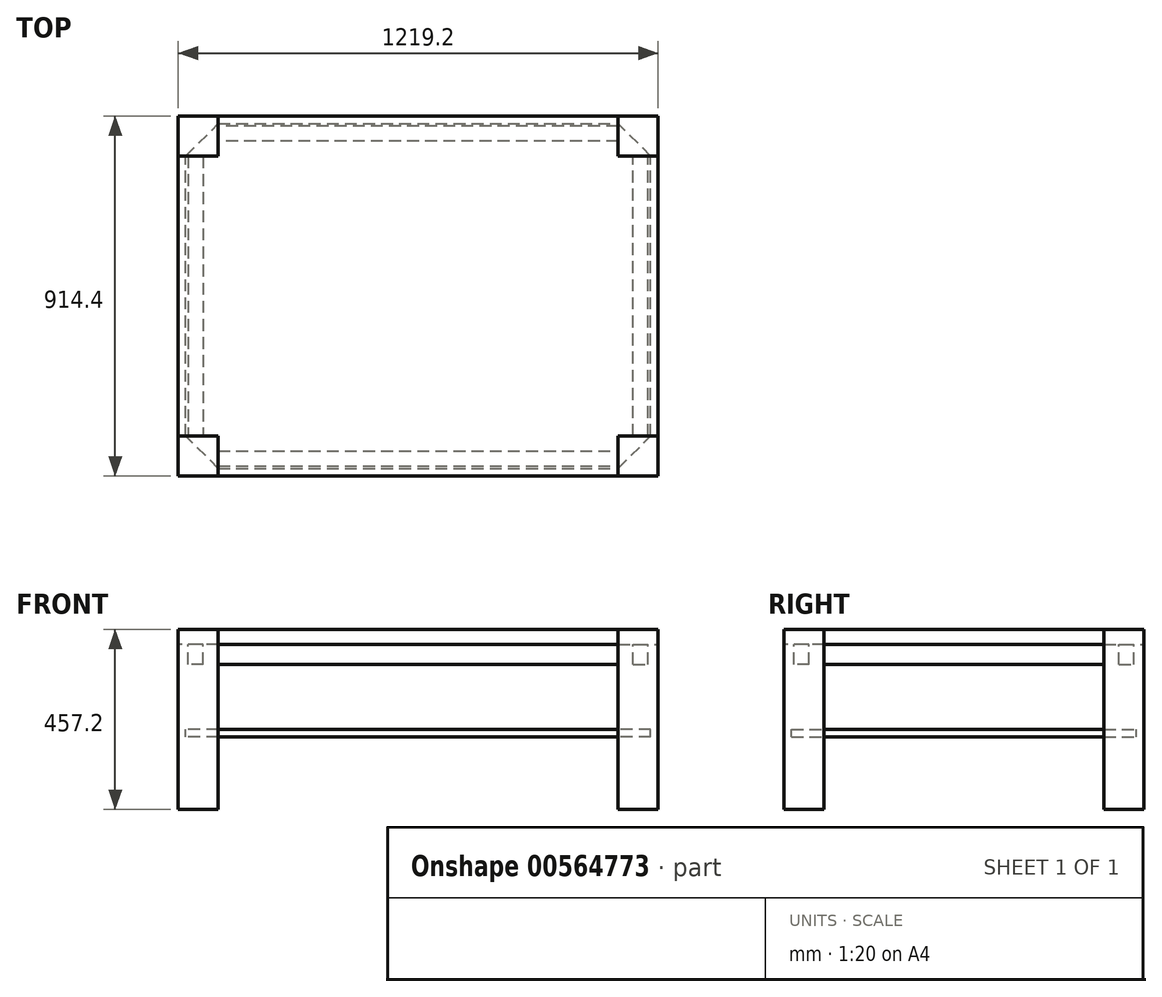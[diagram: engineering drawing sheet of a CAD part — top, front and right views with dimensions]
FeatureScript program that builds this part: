
annotation { "Feature Type Name" : "Feature", "Feature Type Description" : "" }
export const myFeature = defineFeature(function(context is Context, id is Id, definition is map)
    precondition{}
    {
        {
            assignVariable(context, id + "F0", {"name" : "height", "anyValue" : 457.2 * mm});
        }
        {
            assignVariable(context, id + "F1", {"name" : "shelf_height", "anyValue" : 203.2 * mm});
        }
        {
            var Q0;
            Q0=qCreatedBy(makeId("Top.planeOp"),FACE);
            var sketch = newSketch(context, id + "F2", { "sketchPlane" : qUnion([Q0])});
            skPoint(sketch, "E0.middle", {"position": v(0, 0) * mm});
            skLineSegment(sketch, "E1", {"start": v(-609.6, 355.6) * mm, "end": v(-609.6, -355.6) * mm});
            skLineSegment(sketch, "E2", {"start": v(-609.6, -355.6) * mm, "end": v(-508, -355.6) * mm});
            skLineSegment(sketch, "E3", {"start": v(-508, -355.6) * mm, "end": v(-508, -457.2) * mm});
            skLineSegment(sketch, "E4", {"start": v(-508, -457.2) * mm, "end": v(508, -457.2) * mm});
            skLineSegment(sketch, "E5", {"start": v(508, -457.2) * mm, "end": v(508, -355.6) * mm});
            skLineSegment(sketch, "E6", {"start": v(508, -355.6) * mm, "end": v(609.6, -355.6) * mm});
            skLineSegment(sketch, "E7", {"start": v(609.6, -355.6) * mm, "end": v(609.6, 355.6) * mm});
            skLineSegment(sketch, "E8", {"start": v(609.6, 355.6) * mm, "end": v(508, 355.6) * mm});
            skLineSegment(sketch, "E9", {"start": v(508, 355.6) * mm, "end": v(508, 457.2) * mm});
            skLineSegment(sketch, "E10", {"start": v(508, 457.2) * mm, "end": v(-508, 457.2) * mm});
            skLineSegment(sketch, "E11", {"start": v(-508, 457.2) * mm, "end": v(-508, 355.6) * mm});
            skLineSegment(sketch, "E12", {"start": v(-508, 355.6) * mm, "end": v(-609.6, 355.6) * mm});
            skLineSegment(sketch, "E13", {"start": v(-508, 355.6) * mm, "end": v(508, -355.6) * mm, "construction": true});
            skLineSegment(sketch, "E14", {"start": v(508, 355.6) * mm, "end": v(-508, -355.6) * mm, "construction": true});
            skSolve(sketch);
        }
        {
            var Q0;
            Q0 = qSketchRegion(id + "F2", true);
            extrude(context, id + "F3", {"entities" : qUnion([Q0]), "depth" : 38.1 * mm, "offsetDistance" : 25.4 * mm});
        }
        {
            var Q0;
            Q0=makeQuery(id+"F3.opExtrude","CAP_FACE",FACE,{"disambiguationData":[OSD([sQuery(id+"F2.wireOp",EDGE,"E1"),sQuery(id+"F2.wireOp",EDGE,"E2"),sQuery(id+"F2.wireOp",EDGE,"E3"),sQuery(id+"F2.wireOp",EDGE,"E4"),sQuery(id+"F2.wireOp",EDGE,"E5"),sQuery(id+"F2.wireOp",EDGE,"E6"),sQuery(id+"F2.wireOp",EDGE,"E7"),sQuery(id+"F2.wireOp",EDGE,"E8"),sQuery(id+"F2.wireOp",EDGE,"E9"),sQuery(id+"F2.wireOp",EDGE,"E10"),sQuery(id+"F2.wireOp",EDGE,"E11"),sQuery(id+"F2.wireOp",EDGE,"E12")])],"isStart":false});
            var sketch = newSketch(context, id + "F4", { "sketchPlane" : qUnion([Q0])});
            skLineSegment(sketch, "E15.bottom", {"start": v(-609.6, -355.6) * mm, "end": v(-508, -355.6) * mm});
            skLineSegment(sketch, "E15.top", {"start": v(-609.6, -457.2) * mm, "end": v(-508, -457.2) * mm});
            skLineSegment(sketch, "E15.left", {"start": v(-609.6, -355.6) * mm, "end": v(-609.6, -457.2) * mm});
            skLineSegment(sketch, "E15.right", {"start": v(-508, -355.6) * mm, "end": v(-508, -457.2) * mm});
            skLineSegment(sketch, "E16.bottom", {"start": v(508, -457.2) * mm, "end": v(609.6, -457.2) * mm});
            skLineSegment(sketch, "E16.top", {"start": v(508, -355.6) * mm, "end": v(609.6, -355.6) * mm});
            skLineSegment(sketch, "E16.left", {"start": v(508, -457.2) * mm, "end": v(508, -355.6) * mm});
            skLineSegment(sketch, "E16.right", {"start": v(609.6, -457.2) * mm, "end": v(609.6, -355.6) * mm});
            skLineSegment(sketch, "E17.bottom", {"start": v(609.6, 355.6) * mm, "end": v(508, 355.6) * mm});
            skLineSegment(sketch, "E17.top", {"start": v(609.6, 457.2) * mm, "end": v(508, 457.2) * mm});
            skLineSegment(sketch, "E17.left", {"start": v(609.6, 355.6) * mm, "end": v(609.6, 457.2) * mm});
            skLineSegment(sketch, "E17.right", {"start": v(508, 355.6) * mm, "end": v(508, 457.2) * mm});
            skLineSegment(sketch, "E18.bottom", {"start": v(-508, 457.2) * mm, "end": v(-609.6, 457.2) * mm});
            skLineSegment(sketch, "E18.top", {"start": v(-508, 355.6) * mm, "end": v(-609.6, 355.6) * mm});
            skLineSegment(sketch, "E18.left", {"start": v(-508, 457.2) * mm, "end": v(-508, 355.6) * mm});
            skLineSegment(sketch, "E18.right", {"start": v(-609.6, 457.2) * mm, "end": v(-609.6, 355.6) * mm});
            skSolve(sketch);
        }
        {
            var Q0;
            Q0 = qSketchRegion(id + "F4", true);
            extrude(context, id + "F5", {"entities" : qUnion([Q0]), "oppositeDirection" : true, "depth" : getVariable(context, 'height'), "offsetDistance" : 25.4 * mm});
        }
        {
            var Q0;
            Q0=makeQuery(id+"F5.opExtrude","CAP_FACE",FACE,{"disambiguationData":[OSD([sQuery(id+"F4.wireOp",EDGE,"E15.bottom"),sQuery(id+"F4.wireOp",EDGE,"E15.top"),sQuery(id+"F4.wireOp",EDGE,"E15.left"),sQuery(id+"F4.wireOp",EDGE,"E15.right")])],"isStart":false});
            cPlane(context, id + "F6", {"entities" : qUnion([Q0]), "cplaneType" : CPlaneType.OFFSET, "offset" : getVariable(context, 'shelf_height'), "oppositeDirection" : true, "width" : 152.4 * mm, "height" : 152.4 * mm});
        }
        {
            var Q0;
            Q0=qCreatedBy(id+"F6.planeOp",FACE);
            var sketch = newSketch(context, id + "F7", { "sketchPlane" : qUnion([Q0])});
            skLineSegment(sketch, "E19.bottom", {"start": v(-590.5, 438.1) * mm, "end": v(590.5, 438.1) * mm});
            skLineSegment(sketch, "E19.top", {"start": v(-590.5, -438.1) * mm, "end": v(590.5, -438.1) * mm});
            skLineSegment(sketch, "E19.left", {"start": v(-590.5, 438.1) * mm, "end": v(-590.5, -438.1) * mm});
            skLineSegment(sketch, "E19.right", {"start": v(590.5, 438.1) * mm, "end": v(590.5, -438.1) * mm});
            skLineSegment(sketch, "E20", {"start": v(-508, 438.1) * mm, "end": v(-590.5, 355.6) * mm});
            skLineSegment(sketch, "E21", {"start": v(508, 438.1) * mm, "end": v(590.5, 355.6) * mm});
            skLineSegment(sketch, "E22", {"start": v(590.5, -355.6) * mm, "end": v(508, -438.1) * mm});
            skLineSegment(sketch, "E23", {"start": v(-590.5, -355.6) * mm, "end": v(-508, -438.1) * mm});
            skSolve(sketch);
        }
        {
            var Q0;
            {var subQ3=sQuery(id+"F7.wireOp",EDGE,"E20");Q0=makeQuery(id+"F7.imprint","IMPRINT",FACE,{"disambiguationData":[TD([[makeQuery(id+"F7.imprint","IMPRINT",EDGE,{"derivedFrom":subQ3}),1.0]])]});}
            extrude(context, id + "F8", {"entities" : qUnion([Q0]), "depth" : 19.05 * mm, "offsetDistance" : 25.4 * mm});
        }
        {
            var Q0;
            Q0=makeQuery(id+"F3.opExtrude","CAP_FACE",FACE,{"disambiguationData":[OSD([sQuery(id+"F2.wireOp",EDGE,"E1"),sQuery(id+"F2.wireOp",EDGE,"E2"),sQuery(id+"F2.wireOp",EDGE,"E3"),sQuery(id+"F2.wireOp",EDGE,"E4"),sQuery(id+"F2.wireOp",EDGE,"E5"),sQuery(id+"F2.wireOp",EDGE,"E6"),sQuery(id+"F2.wireOp",EDGE,"E7"),sQuery(id+"F2.wireOp",EDGE,"E8"),sQuery(id+"F2.wireOp",EDGE,"E9"),sQuery(id+"F2.wireOp",EDGE,"E10"),sQuery(id+"F2.wireOp",EDGE,"E11"),sQuery(id+"F2.wireOp",EDGE,"E12")])],"isStart":true});
            var sketch = newSketch(context, id + "F9", { "sketchPlane" : qUnion([Q0])});
            skLineSegment(sketch, "E24.bottom", {"start": v(-508, 431.8) * mm, "end": v(508, 431.8) * mm});
            skLineSegment(sketch, "E24.top", {"start": v(-508, 393.7) * mm, "end": v(508, 393.7) * mm});
            skLineSegment(sketch, "E24.left", {"start": v(-508, 431.8) * mm, "end": v(-508, 393.7) * mm});
            skLineSegment(sketch, "E24.right", {"start": v(508, 431.8) * mm, "end": v(508, 393.7) * mm});
            skLineSegment(sketch, "E25.bottom", {"start": v(584.2, 355.6) * mm, "end": v(546.1, 355.6) * mm});
            skLineSegment(sketch, "E25.top", {"start": v(584.2, -355.6) * mm, "end": v(546.1, -355.6) * mm});
            skLineSegment(sketch, "E25.left", {"start": v(584.2, 355.6) * mm, "end": v(584.2, -355.6) * mm});
            skLineSegment(sketch, "E25.right", {"start": v(546.1, 355.6) * mm, "end": v(546.1, -355.6) * mm});
            skLineSegment(sketch, "E26.bottom", {"start": v(508, -393.7) * mm, "end": v(-508, -393.7) * mm});
            skLineSegment(sketch, "E26.top", {"start": v(508, -431.8) * mm, "end": v(-508, -431.8) * mm});
            skLineSegment(sketch, "E26.left", {"start": v(508, -393.7) * mm, "end": v(508, -431.8) * mm});
            skLineSegment(sketch, "E26.right", {"start": v(-508, -393.7) * mm, "end": v(-508, -431.8) * mm});
            skLineSegment(sketch, "E27.bottom", {"start": v(-584.2, -355.6) * mm, "end": v(-546.1, -355.6) * mm});
            skLineSegment(sketch, "E27.top", {"start": v(-584.2, 355.6) * mm, "end": v(-546.1, 355.6) * mm});
            skLineSegment(sketch, "E27.left", {"start": v(-584.2, -355.6) * mm, "end": v(-584.2, 355.6) * mm});
            skLineSegment(sketch, "E27.right", {"start": v(-546.1, -355.6) * mm, "end": v(-546.1, 355.6) * mm});
            skLineSegment(sketch, "E28", {"start": v(-508, 457.2) * mm, "end": v(-508, 431.8) * mm, "construction": true});
            skLineSegment(sketch, "E29", {"start": v(-609.6, 355.6) * mm, "end": v(-584.2, 355.6) * mm, "construction": true});
            skLineSegment(sketch, "E30", {"start": v(-508, -457.2) * mm, "end": v(-508, -431.8) * mm, "construction": true});
            skLineSegment(sketch, "E31", {"start": v(609.6, 355.6) * mm, "end": v(584.2, 355.6) * mm, "construction": true});
            skSolve(sketch);
        }
        {
            var Q0;
            Q0 = qSketchRegion(id + "F9", true);
            extrude(context, id + "F10", {"entities" : qUnion([Q0]), "depth" : 50.8 * mm, "offsetDistance" : 25.4 * mm});
        }
    });
